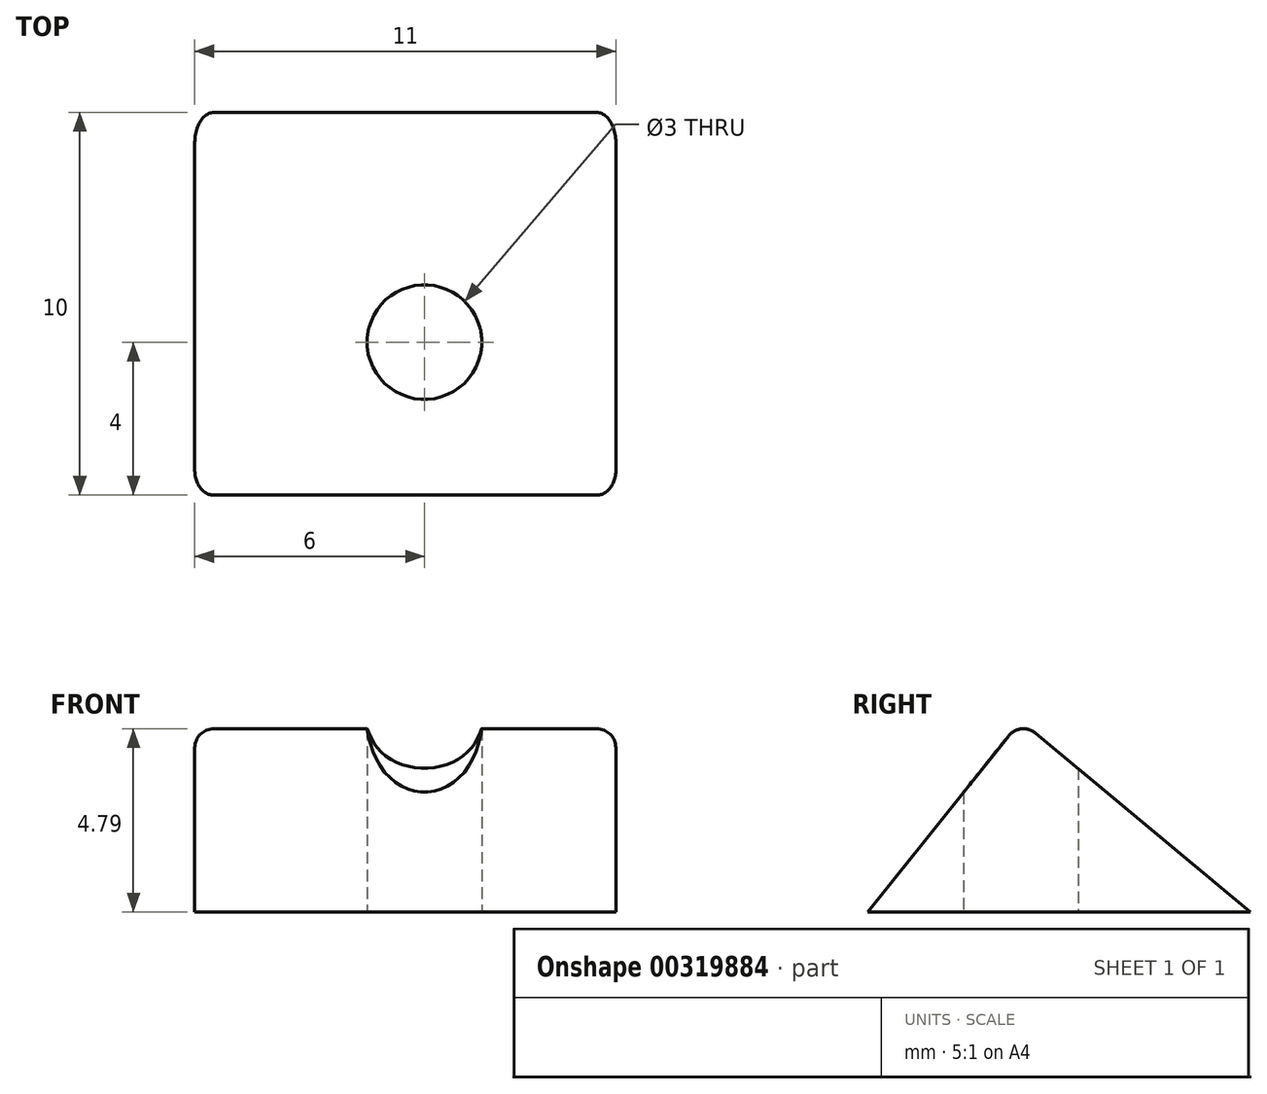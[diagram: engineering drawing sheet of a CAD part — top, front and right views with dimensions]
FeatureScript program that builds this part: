
annotation { "Feature Type Name" : "Feature", "Feature Type Description" : "" }
export const myFeature = defineFeature(function(context is Context, id is Id, definition is map)
    precondition{}
    {
        {
            var Q0;
            Q0=qCreatedBy(makeId("Right.planeOp"),FACE);
            var sketch = newSketch(context, id + "F0", { "sketchPlane" : qUnion([Q0])});
            skLineSegment(sketch, "E0", {"start": v(0, 0) * mm, "end": v(10, 0) * mm});
            skLineSegment(sketch, "E1", {"start": v(10, 0) * mm, "end": v(10, 5) * mm});
            skLineSegment(sketch, "E2", {"start": v(10, 5) * mm, "end": v(0, 5) * mm});
            skLineSegment(sketch, "E3", {"start": v(0, 5) * mm, "end": v(0, 0) * mm});
            skLineSegment(sketch, "E4", {"start": v(4, 0) * mm, "end": v(4, 5) * mm});
            skLineSegment(sketch, "E5", {"start": v(4, 5) * mm, "end": v(0, 0) * mm});
            skLineSegment(sketch, "E6", {"start": v(4, 5) * mm, "end": v(10, 0) * mm});
            skLineSegment(sketch, "E7", {"start": v(10, 0) * mm, "end": v(4, 0) * mm});
            skSolve(sketch);
        }
        {
            var Q0;
            Q0=makeQuery(id+"F0.imprint","IMPRINT",FACE,{"disambiguationData":[TD([[makeQuery(id+"F0.imprint","IMPRINT",EDGE,{"derivedFrom":sQuery(id+"F0.wireOp",EDGE,"h0lS08ow-zRtw-w6tf-FX9q-PSKdkQJl8r6e")}),1.0]])]});
            var Q1;
            Q1=makeQuery(id+"F0.imprint","IMPRINT",FACE,{"disambiguationData":[TD([[makeQuery(id+"F0.imprint","IMPRINT",EDGE,{"derivedFrom":sQuery(id+"F0.wireOp",EDGE,"E0")}),1.0]])]});
            var Q2;
            Q2=makeQuery(id+"F0.imprint","IMPRINT",FACE,{"disambiguationData":[TD([[makeQuery(id+"F0.imprint","IMPRINT",EDGE,{"derivedFrom":sQuery(id+"F0.wireOp",EDGE,"E4")}),-1.0]])]});
            extrude(context, id + "F1", {"entities" : qUnion([Q0, Q1, Q2]), "oppositeDirection" : true, "depth" : 11 * mm});
        }
        {
            var Q0;
            Q0=makeQuery(id+"F1.opExtrude","SWEPT_EDGE",EDGE,{"disambiguationData":[OSD([sQuery(id+"F0.wireOp",EDGE,"E2"),sQuery(id+"F0.wireOp",EDGE,"E4"),sQuery(id+"F0.wireOp",EDGE,"E5"),sQuery(id+"F0.wireOp",EDGE,"E6")])]});
            fillet(context, id + "F2", {"entities" : qUnion([Q0]), "radius" : .5 * mm, "tangentPropagation" : true, "allowEdgeOverflow" : false});
        }
        {
            var Q0;
            Q0=makeQuery(id+"F1.opExtrude","SWEPT_FACE",FACE,{"disambiguationData":[OSD([sQuery(id+"F0.wireOp",EDGE,"E0"),sQuery(id+"F0.wireOp",EDGE,"h0lS08ow-zRtw-w6tf-FX9q-PSKdkQJl8r6e")])]});
            var sketch = newSketch(context, id + "F3", { "sketchPlane" : qUnion([Q0])});
            skLineSegment(sketch, "E8", {"start": v(0, 0) * mm, "end": v(0, -4) * mm});
            skLineSegment(sketch, "E9", {"start": v(0, -4) * mm, "end": v(0, -10) * mm});
            skLineSegment(sketch, "E10", {"start": v(0, -4) * mm, "end": v(-5, -4) * mm});
            skSolve(sketch);
        }
        {
            var Q0;
            Q0=sQuery(id+"F3.wireOp",VERTEX,"Xtzmw7LG-RXL7-amLN-lJNL-RaqkvvplooiG.end");
            var Q1;
            Q1=sQuery(id+"F3.wireOp",VERTEX,"E10.end");
            var Q2;
            Q2=makeQuery(id+"F1.opExtrude","SWEPT_BODY",BODY,{"disambiguationData":[OSD([sQuery(id+"F0.wireOp",EDGE,"E0"),sQuery(id+"F0.wireOp",EDGE,"h0lS08ow-zRtw-w6tf-FX9q-PSKdkQJl8r6e"),sQuery(id+"F0.wireOp",EDGE,"E5"),sQuery(id+"F0.wireOp",EDGE,"E6")])]});
            hole(context, id + "F4", {"style" : HoleStyle.SIMPLE, "endStyle" : HoleEndStyle.BLIND, "holeDiameter" : 3 * mm, "holeDepth" : 10 * mm, "tappedDepth" : 12 * mm, "tapClearance" : 3, "locations" : qUnion([Q0, Q1]), "scope" : qUnion([Q2])});
        }
        {
            var Q0;
            Q0=makeQuery(id+"F4.hole-0.boolean.opBoolean","INTERSECT",EDGE,{"derivedFrom":[makeQuery(id+"F1.opExtrude","SWEPT_FACE",FACE,{"disambiguationData":[OSD([sQuery(id+"F0.wireOp",EDGE,"E5")])]}),makeQuery(id+"F4.hole-0.opRevolve","SWEPT_FACE",FACE,{"disambiguationData":[OSD([sQuery(id+"F4.hole-0.sketch.wireOp",EDGE,"core_line_2")])]})]});
            var Q1;
            Q1=makeQuery(id+"F4.hole-0.boolean.opBoolean","INTERSECT",EDGE,{"derivedFrom":[makeQuery(id+"F1.opExtrude","SWEPT_FACE",FACE,{"disambiguationData":[OSD([sQuery(id+"F0.wireOp",EDGE,"E6")])]}),makeQuery(id+"F4.hole-0.opRevolve","SWEPT_FACE",FACE,{"disambiguationData":[OSD([sQuery(id+"F4.hole-0.sketch.wireOp",EDGE,"core_line_2")])]})]});
            var Q2;
            Q2=makeQuery(id+"F1.opExtrude","CAP_EDGE",EDGE,{"disambiguationData":[OSD([sQuery(id+"F0.wireOp",EDGE,"E5")])],"isStart":true});
            var Q3;
            Q3=makeQuery(id+"F1.opExtrude","CAP_EDGE",EDGE,{"disambiguationData":[OSD([sQuery(id+"F0.wireOp",EDGE,"E6")])],"isStart":false});
            fillet(context, id + "F5", {"entities" : qUnion([Q0, Q1, Q2, Q3]), "radius" : .5 * mm, "tangentPropagation" : true, "allowEdgeOverflow" : false});
        }
    });
